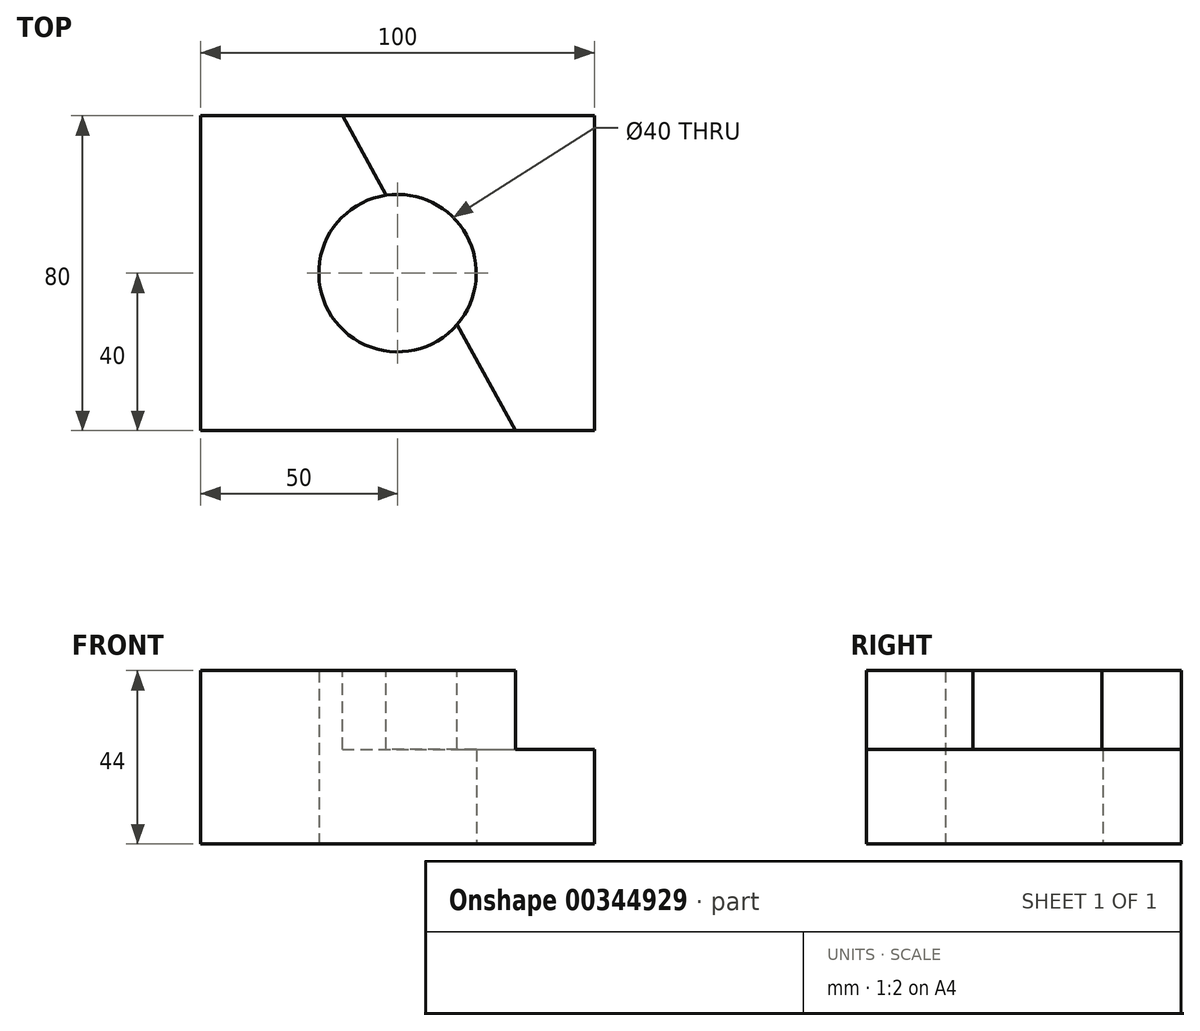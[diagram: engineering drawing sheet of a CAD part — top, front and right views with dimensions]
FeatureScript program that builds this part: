
annotation { "Feature Type Name" : "Feature", "Feature Type Description" : "" }
export const myFeature = defineFeature(function(context is Context, id is Id, definition is map)
    precondition{}
    {
        {
            var Q0;
            Q0=qCreatedBy(makeId("Top.planeOp"),FACE);
            var sketch = newSketch(context, id + "F0", { "sketchPlane" : qUnion([Q0])});
            skLineSegment(sketch, "E0.bottom", {"start": v(-50, 40) * mm, "end": v(50, 40) * mm});
            skLineSegment(sketch, "E0.top", {"start": v(-50, -40) * mm, "end": v(50, -40) * mm});
            skLineSegment(sketch, "E0.left", {"start": v(-50, 40) * mm, "end": v(-50, -40) * mm});
            skLineSegment(sketch, "E0.right", {"start": v(50, 40) * mm, "end": v(50, -40) * mm});
            skLineSegment(sketch, "E1", {"start": v(-50, 0) * mm, "end": v(0, 0) * mm, "construction": true});
            skLineSegment(sketch, "E2", {"start": v(0, 40) * mm, "end": v(0, 0) * mm, "construction": true});
            skCircle(sketch, "E3", {"center": v(0, 0) * mm, "radius": 20 * mm});
            skLineSegment(sketch, "E4", {"start": v(-50, -40) * mm, "end": v(30, -40) * mm, "construction": true});
            skLineSegment(sketch, "E5", {"start": v(-50, 40) * mm, "end": v(-14, 40) * mm, "construction": true});
            skLineSegment(sketch, "E6", {"start": v(-14, 40) * mm, "end": v(30, -40) * mm, "construction": true});
            skSolve(sketch);
        }
        {
            var Q0;
            Q0=makeQuery(id+"F0.imprint","IMPRINT",FACE,{"disambiguationData":[TD([[makeQuery(id+"F0.imprint","IMPRINT",EDGE,{"derivedFrom":sQuery(id+"F0.wireOp",EDGE,"E0.bottom")}),-1.0]])]});
            extrude(context, id + "F1", {"entities" : qUnion([Q0]), "depth" : 44 * mm});
        }
        {
            var Q0;
            Q0=makeQuery(id+"F1.opExtrude","CAP_FACE",FACE,{"disambiguationData":[OSD([sQuery(id+"F0.wireOp",EDGE,"E0.bottom"),sQuery(id+"F0.wireOp",EDGE,"E0.top"),sQuery(id+"F0.wireOp",EDGE,"E0.left"),sQuery(id+"F0.wireOp",EDGE,"E0.right"),sQuery(id+"F0.wireOp",EDGE,"E3")])],"isStart":false});
            var sketch = newSketch(context, id + "F2", { "sketchPlane" : qUnion([Q0])});
            skLineSegment(sketch, "E7.0", {"start": v(-14, 40) * mm, "end": v(30, -40) * mm});
            skLineSegment(sketch, "E8.1", {"start": v(-14, 40) * mm, "end": v(50, 40) * mm});
            skLineSegment(sketch, "E9.0", {"start": v(50, 40) * mm, "end": v(50, -40) * mm});
            skLineSegment(sketch, "E10.0", {"start": v(30, -40) * mm, "end": v(50, -40) * mm});
            skPoint(sketch, "E11.orphan", {"position": v(-50, 40) * mm});
            skPoint(sketch, "E12.orphan", {"position": v(-50, -40) * mm});
            skSolve(sketch);
        }
        {
            var Q0;
            {var subQ0=sQuery(id+"F2.wireOp",EDGE,"E8.1");Q0=makeQuery(id+"F2.imprint","IMPRINT",FACE,{"disambiguationData":[TD([[makeQuery(id+"F2.imprint","IMPRINT",EDGE,{"derivedFrom":subQ0}),-1.0]])]});}
            extrude(context, id + "F3", {"entities" : qUnion([Q0]), "operationType" : NewBodyOperationType.REMOVE, "oppositeDirection" : true, "depth" : (44 - 24) * mm});
        }
    });
